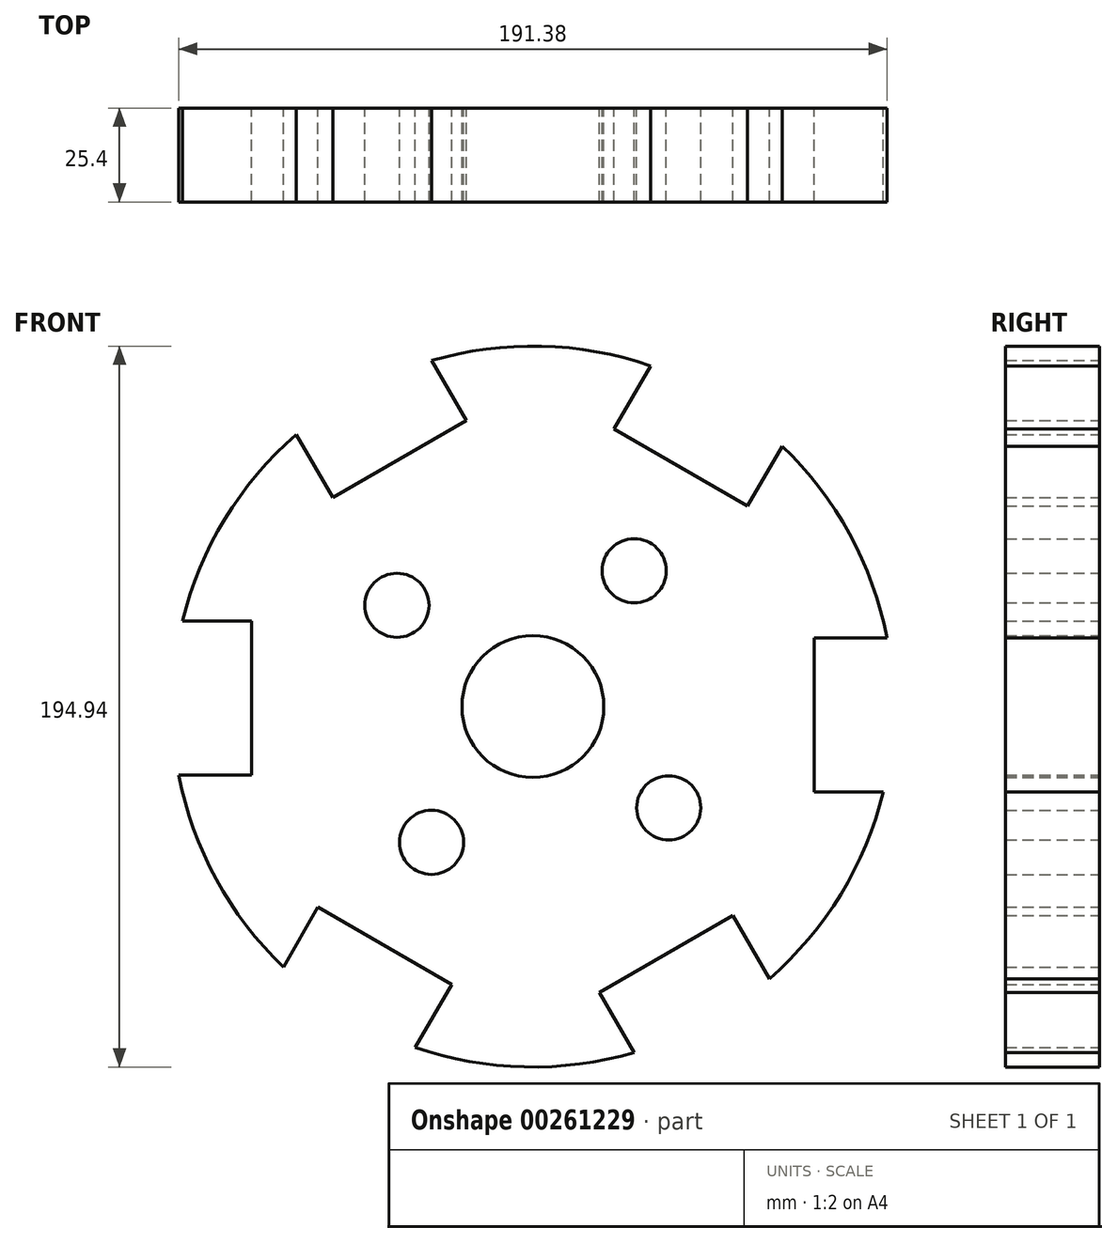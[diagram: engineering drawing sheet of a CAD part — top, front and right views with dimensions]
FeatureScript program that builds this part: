
annotation { "Feature Type Name" : "Feature", "Feature Type Description" : "" }
export const myFeature = defineFeature(function(context is Context, id is Id, definition is map)
    precondition{}
    {
        {
            var Q0;
            Q0=qCreatedBy(makeId("Front.planeOp"),FACE);
            var sketch = newSketch(context, id + "F0", { "sketchPlane" : qUnion([Q0])});
            skCircle(sketch, "E0", {"center": v(0, 0) * mm, "radius": 19.17 * mm});
            skCircle(sketch, "E1", {"center": v(-36.72, 27.38) * mm, "radius": 8.67 * mm});
            skCircle(sketch, "E2.1.0", {"center": v(-27.38, -36.72) * mm, "radius": 8.67 * mm});
            skCircle(sketch, "E2.2.0", {"center": v(36.72, -27.38) * mm, "radius": 8.67 * mm});
            skCircle(sketch, "E2.3.0", {"center": v(27.38, 36.72) * mm, "radius": 8.67 * mm});
            skCircle(sketch, "E3", {"center": v(0, 0) * mm, "radius": 97.47 * mm});
            skLineSegment(sketch, "E4", {"start": v(-94.69, 23.13) * mm, "end": v(-76, 23.13) * mm});
            skLineSegment(sketch, "E5", {"start": v(-76, 23.13) * mm, "end": v(-76, -18.57) * mm});
            skLineSegment(sketch, "E6", {"start": v(-76, -18.57) * mm, "end": v(-95.69, -18.57) * mm});
            skLineSegment(sketch, "E7.1.1", {"start": v(-67.38, -70.44) * mm, "end": v(-58.04, -54.26) * mm});
            skLineSegment(sketch, "E7.1.2", {"start": v(-21.92, -75.1) * mm, "end": v(-31.76, -92.15) * mm});
            skLineSegment(sketch, "E7.1.3", {"start": v(-58.04, -54.26) * mm, "end": v(-21.92, -75.1) * mm});
            skLineSegment(sketch, "E7.2.1", {"start": v(27.31, -93.57) * mm, "end": v(17.97, -77.39) * mm});
            skLineSegment(sketch, "E7.2.2", {"start": v(54.08, -56.54) * mm, "end": v(63.92, -73.58) * mm});
            skLineSegment(sketch, "E7.2.3", {"start": v(17.97, -77.39) * mm, "end": v(54.08, -56.54) * mm});
            skArc(sketch, "E7.3.0", {"start": v(31.76, 92.15) * mm, "mid": v(-85.56, -46.7) * mm, "end": v(94.69, -23.13) * mm});
            skLineSegment(sketch, "E7.3.1", {"start": v(94.69, -23.13) * mm, "end": v(76, -23.13) * mm});
            skLineSegment(sketch, "E7.3.2", {"start": v(76, 18.57) * mm, "end": v(95.69, 18.57) * mm});
            skLineSegment(sketch, "E7.3.3", {"start": v(76, -23.13) * mm, "end": v(76, 18.57) * mm});
            skArc(sketch, "E7.4.0", {"start": v(-48.74, -84.41) * mm, "mid": v(-40.44, -88.69) * mm, "end": v(-31.76, -92.15) * mm});
            skLineSegment(sketch, "E7.4.1", {"start": v(67.38, 70.44) * mm, "end": v(58.04, 54.26) * mm});
            skLineSegment(sketch, "E7.4.2", {"start": v(21.92, 75.1) * mm, "end": v(31.76, 92.15) * mm});
            skLineSegment(sketch, "E7.4.3", {"start": v(58.04, 54.26) * mm, "end": v(21.92, 75.1) * mm});
            skLineSegment(sketch, "E7.5.1", {"start": v(-27.31, 93.57) * mm, "end": v(-17.97, 77.39) * mm});
            skLineSegment(sketch, "E7.5.2", {"start": v(-54.08, 56.54) * mm, "end": v(-63.92, 73.58) * mm});
            skLineSegment(sketch, "E7.5.3", {"start": v(-17.97, 77.39) * mm, "end": v(-54.08, 56.54) * mm});
            skArc(sketch, "E8.trimOffspring", {"start": v(95.69, 18.57) * mm, "mid": v(85.56, 46.7) * mm, "end": v(67.38, 70.44) * mm});
            skArc(sketch, "E9.trimOffspring", {"start": v(63.92, -73.58) * mm, "mid": v(83.22, -50.75) * mm, "end": v(94.69, -23.13) * mm});
            skArc(sketch, "E10.trimOffspring", {"start": v(-63.92, 73.58) * mm, "mid": v(-97.44, 2.34) * mm, "end": v(-67.38, -70.44) * mm});
            skArc(sketch, "E11.trimOffspring", {"start": v(-48.74, -84.41) * mm, "mid": v(-11.65, -96.77) * mm, "end": v(27.31, -93.57) * mm});
            skArc(sketch, "E12.trimOffspring", {"start": v(95.69, 18.57) * mm, "mid": v(-46.7, 85.56) * mm, "end": v(-67.38, -70.44) * mm});
            skSolve(sketch);
        }
        {
            var Q0;
            Q0=makeQuery(id+"F0.imprint","IMPRINT",FACE,{"disambiguationData":[TD([[makeQuery(id+"F0.imprint","IMPRINT",EDGE,{"derivedFrom":sQuery(id+"F0.wireOp",EDGE,"E0")}),-1.0]])]});
            extrude(context, id + "F1", {"entities" : qUnion([Q0]), "depth" : 25.4 * mm});
        }
    });
